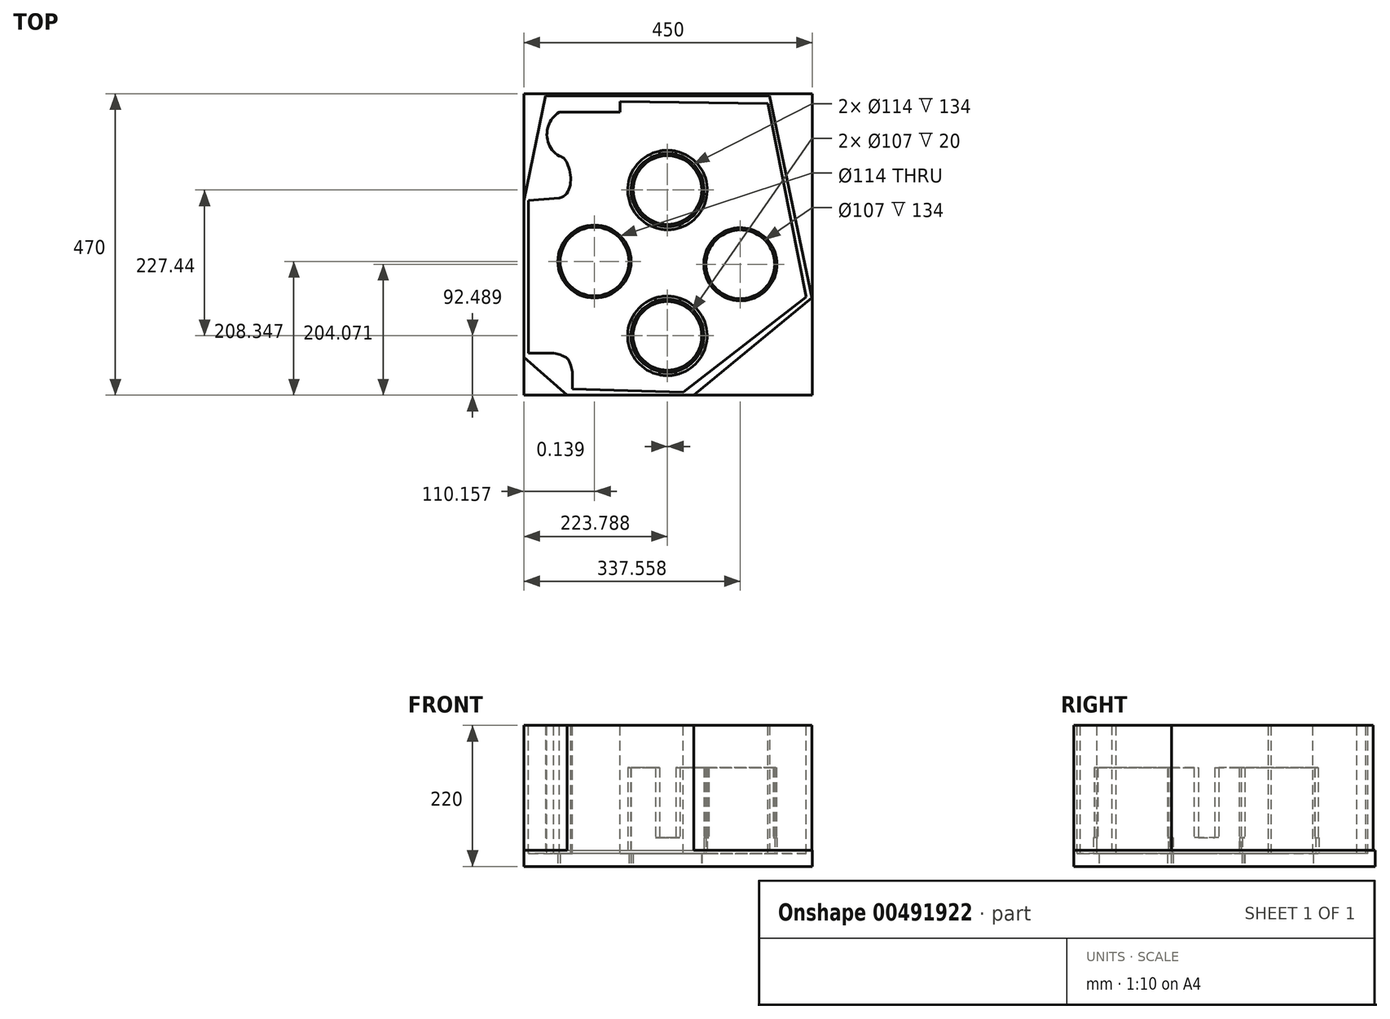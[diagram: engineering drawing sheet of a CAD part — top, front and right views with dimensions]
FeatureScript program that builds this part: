
annotation { "Feature Type Name" : "Feature", "Feature Type Description" : "" }
export const myFeature = defineFeature(function(context is Context, id is Id, definition is map)
    precondition{}
    {
        {
            var Q0;
            Q0=qCreatedBy(makeId("Top.planeOp"),FACE);
            var sketch = newSketch(context, id + "F0", { "sketchPlane" : qUnion([Q0])});
            skLineSegment(sketch, "E0", {"start": v(-238.56, 7.34) * mm, "end": v(-238.56, -236.7) * mm});
            skLineSegment(sketch, "E1", {"start": v(-171.3, -295.66) * mm, "end": v(26.17, -295.66) * mm});
            skLineSegment(sketch, "E2", {"start": v(-204.78, 171.15) * mm, "end": v(144.4, 171.15) * mm});
            skLineSegment(sketch, "E3", {"start": v(-238.56, 7.34) * mm, "end": v(-204.78, 171.15) * mm});
            skLineSegment(sketch, "E4", {"start": v(-238.56, -236.7) * mm, "end": v(-171.3, -295.66) * mm});
            skLineSegment(sketch, "E5", {"start": v(26.17, -295.66) * mm, "end": v(210.43, -143.64) * mm});
            skLineSegment(sketch, "E6", {"start": v(210.43, -143.64) * mm, "end": v(144.4, 171.15) * mm});
            skSolve(sketch);
        }
        {
            var Q0;
            Q0=qSketchRegion(id+"F0",true);
            extrude(context, id + "F1", {"entities" : qUnion([Q0]), "depth" : 220 * mm});
        }
        {
            var Q0;
            Q0=makeQuery(id+"F1.opExtrude","CAP_FACE",FACE,{"disambiguationData":[OSD([sQuery(id+"F0.wireOp",EDGE,"E0"),sQuery(id+"F0.wireOp",EDGE,"E1"),sQuery(id+"F0.wireOp",EDGE,"E2"),sQuery(id+"F0.wireOp",EDGE,"E3"),sQuery(id+"F0.wireOp",EDGE,"E4"),sQuery(id+"F0.wireOp",EDGE,"E5"),sQuery(id+"F0.wireOp",EDGE,"E6")])],"isStart":false});
            var sketch = newSketch(context, id + "F2", { "sketchPlane" : qUnion([Q0])});
            skLineSegment(sketch, "E7", {"start": v(-88.7, 162.55) * mm, "end": v(141.95, 159.17) * mm});
            skLineSegment(sketch, "E8", {"start": v(141.95, 159.17) * mm, "end": v(201.83, -142.4) * mm});
            skLineSegment(sketch, "E9", {"start": v(201.83, -142.4) * mm, "end": v(10.2, -291.05) * mm});
            skLineSegment(sketch, "E10", {"start": v(10.2, -291.05) * mm, "end": v(-163.01, -285.83) * mm});
            skLineSegment(sketch, "E11", {"start": v(-231.2, -229.93) * mm, "end": v(-231.2, 7.77) * mm});
            skLineSegment(sketch, "E12", {"start": v(-88.7, 162.55) * mm, "end": v(-88.7, 145.66) * mm});
            skLineSegment(sketch, "E13", {"start": v(-88.7, 145.66) * mm, "end": v(-182.98, 145.66) * mm});
            skFitSpline(sketch, "E14", {"points": [v(-182.98, 145.66) * mm, v(-182.98, 77.18) * mm], "startDerivative": vector(-73.7, -41.46) * mm, "endDerivative": vector(82.92, -44.22) * mm});
            skFitSpline(sketch, "E15", {"points": [v(-182.98, 77.18) * mm, v(-182.98, 12.07) * mm], "startDerivative": vector(54.36, -6.45) * mm, "endDerivative": vector(-83.84, -15.66) * mm});
            skLineSegment(sketch, "E16", {"start": v(-182.98, 12.07) * mm, "end": v(-231.2, 7.77) * mm});
            skLineSegment(sketch, "E17", {"start": v(-231.2, -229.93) * mm, "end": v(-191.88, -229.93) * mm});
            skLineSegment(sketch, "E18", {"start": v(-163.01, -285.83) * mm, "end": v(-163.01, -259.42) * mm});
            skFitSpline(sketch, "E19", {"points": [v(-191.88, -229.93) * mm, v(-163.01, -259.42) * mm], "startDerivative": vector(70.94, -20.27) * mm, "endDerivative": vector(15.66, -68.18) * mm});
            skSolve(sketch);
        }
        {
            var Q0;
            Q0=qCreatedBy(makeId("Top.planeOp"),FACE);
            var sketch = newSketch(context, id + "F3", { "sketchPlane" : qUnion([Q0])});
            skLineSegment(sketch, "E20.bottom", {"start": v(-238.56, -295.66) * mm, "end": v(211.44, -295.66) * mm});
            skLineSegment(sketch, "E20.top", {"start": v(-238.56, 174.34) * mm, "end": v(211.44, 174.34) * mm});
            skLineSegment(sketch, "E20.left", {"start": v(-238.56, -295.66) * mm, "end": v(-238.56, 174.34) * mm});
            skLineSegment(sketch, "E20.right", {"start": v(211.44, -295.66) * mm, "end": v(211.44, 174.34) * mm});
            skSolve(sketch);
        }
        {
            var Q0;
            Q0=makeQuery(id+"F3.imprint","IMPRINT",FACE,{"disambiguationData":[TD([[makeQuery(id+"F3.imprint","IMPRINT",EDGE,{"derivedFrom":sQuery(id+"F3.wireOp",EDGE,"E20.bottom")}),1.0]])]});
            extrude(context, id + "F4", {"entities" : qUnion([Q0]), "operationType" : NewBodyOperationType.ADD, "depth" : 25 * mm});
        }
        {
            var Q0;
            Q0=qSketchRegion(id+"F2",true);
            extrude(context, id + "F5", {"entities" : qUnion([Q0]), "operationType" : NewBodyOperationType.REMOVE, "oppositeDirection" : true, "depth" : 200 * mm});
        }
        {
            var Q0;
            Q0=qCreatedBy(makeId("Top.planeOp"),FACE);
            var sketch = newSketch(context, id + "F6", { "sketchPlane" : qUnion([Q0])});
            skCircle(sketch, "E21", {"center": v(-14.63, 24.27) * mm, "radius": 57 * mm});
            skCircle(sketch, "E22.0", {"center": v(-14.63, 24.27) * mm, "radius": 62 * mm});
            skLineSegment(sketch, "E23", {"start": v(-103, -176.05) * mm, "end": v(74.3, -2.16) * mm});
            skLineSegment(sketch, "E24", {"start": v(-102.43, 0) * mm, "end": v(76.04, -181.98) * mm});
            skCircle(sketch, "E25.MirrorC", {"center": v(99, -91.59) * mm, "radius": 57 * mm});
            skCircle(sketch, "E26.MirrorC", {"center": v(99, -91.59) * mm, "radius": 62 * mm});
            skCircle(sketch, "E27.MirrorC", {"center": v(-128.4, -87.31) * mm, "radius": 62 * mm});
            skCircle(sketch, "E28.MirrorC", {"center": v(-128.4, -87.31) * mm, "radius": 57 * mm});
            skCircle(sketch, "E29.MirrorC", {"center": v(-14.77, -203.17) * mm, "radius": 62 * mm});
            skCircle(sketch, "E30.MirrorC", {"center": v(-14.77, -203.17) * mm, "radius": 57 * mm});
            skCircle(sketch, "E31", {"center": v(-14.63, 24.27) * mm, "radius": 53.5 * mm});
            skCircle(sketch, "E32.MirrorC", {"center": v(-128.4, -87.31) * mm, "radius": 53.5 * mm});
            skCircle(sketch, "E33.MirrorC", {"center": v(99, -91.59) * mm, "radius": 53.5 * mm});
            skCircle(sketch, "E34.MirrorC", {"center": v(-14.77, -203.17) * mm, "radius": 53.5 * mm});
            skSolve(sketch);
        }
        {
            var Q0;
            Q0=makeQuery(id+"F6.imprint","IMPRINT",FACE,{"disambiguationData":[TD([[makeQuery(id+"F6.imprint","IMPRINT",EDGE,{"derivedFrom":sQuery(id+"F6.wireOp",EDGE,"E31")}),1.0]])]});
            var Q1;
            Q1=makeQuery(id+"F6.imprint","IMPRINT",FACE,{"disambiguationData":[TD([[makeQuery(id+"F6.imprint","IMPRINT",EDGE,{"derivedFrom":sQuery(id+"F6.wireOp",EDGE,"E32.MirrorC")}),-1.0]])]});
            var Q2;
            Q2=makeQuery(id+"F6.imprint","IMPRINT",FACE,{"disambiguationData":[TD([[makeQuery(id+"F6.imprint","IMPRINT",EDGE,{"derivedFrom":sQuery(id+"F6.wireOp",EDGE,"E34.MirrorC")}),1.0]])]});
            var Q3;
            Q3=makeQuery(id+"F6.imprint","IMPRINT",FACE,{"disambiguationData":[TD([[makeQuery(id+"F6.imprint","IMPRINT",EDGE,{"derivedFrom":sQuery(id+"F6.wireOp",EDGE,"E33.MirrorC")}),-1.0]])]});
            extrude(context, id + "F7", {"entities" : qUnion([Q0, Q1, Q2, Q3]), "operationType" : NewBodyOperationType.REMOVE, "endBound" : BoundingType.UP_TO_NEXT, "depth" : 25 * mm});
        }
        {
            var Q0;
            Q0=makeQuery(id+"F6.imprint","IMPRINT",FACE,{"disambiguationData":[TD([[makeQuery(id+"F6.imprint","IMPRINT",EDGE,{"derivedFrom":sQuery(id+"F6.wireOp",EDGE,"E25.MirrorC")}),1.0]])]});
            var Q1;
            Q1=makeQuery(id+"F6.imprint","IMPRINT",FACE,{"disambiguationData":[TD([[makeQuery(id+"F6.imprint","IMPRINT",EDGE,{"derivedFrom":sQuery(id+"F6.wireOp",EDGE,"E21")}),-1.0]])]});
            var Q2;
            Q2=makeQuery(id+"F6.imprint","IMPRINT",FACE,{"disambiguationData":[TD([[makeQuery(id+"F6.imprint","IMPRINT",EDGE,{"derivedFrom":sQuery(id+"F6.wireOp",EDGE,"E27.MirrorC")}),-1.0]])]});
            var Q3;
            Q3=makeQuery(id+"F6.imprint","IMPRINT",FACE,{"disambiguationData":[TD([[makeQuery(id+"F6.imprint","IMPRINT",EDGE,{"derivedFrom":sQuery(id+"F6.wireOp",EDGE,"E29.MirrorC")}),1.0]])]});
            extrude(context, id + "F8", {"entities" : qUnion([Q0, Q1, Q2, Q3]), "operationType" : NewBodyOperationType.ADD, "depth" : 154 * mm});
        }
        {
            var Q0;
            Q0=makeQuery(id+"F1.opExtrude","CAP_FACE",FACE,{"disambiguationData":[OSD([sQuery(id+"F0.wireOp",EDGE,"E0"),sQuery(id+"F0.wireOp",EDGE,"E1"),sQuery(id+"F0.wireOp",EDGE,"E2"),sQuery(id+"F0.wireOp",EDGE,"E3"),sQuery(id+"F0.wireOp",EDGE,"E4"),sQuery(id+"F0.wireOp",EDGE,"E5"),sQuery(id+"F0.wireOp",EDGE,"E6")])],"isStart":false});
            var sketch = newSketch(context, id + "F9", { "sketchPlane" : qUnion([Q0])});
            skLineSegment(sketch, "E35", {"start": v(-14.37, 55.87) * mm, "end": v(-14.37, -234.54) * mm, "construction": true});
            skLineSegment(sketch, "E36", {"start": v(-153.35, -89.05) * mm, "end": v(136.38, -89.05) * mm, "construction": true});
            skPoint(sketch, "E37.center", {"position": v(-14.37, -89.05) * mm});
            skLineSegment(sketch, "E38.bottom", {"start": v(-33.62, -89.05) * mm, "end": v(4.88, -89.05) * mm});
            skLineSegment(sketch, "E38.top", {"start": v(-33.62, 14.6) * mm, "end": v(4.88, 14.6) * mm});
            skLineSegment(sketch, "E38.left", {"start": v(-33.62, -89.05) * mm, "end": v(-33.62, 14.6) * mm});
            skLineSegment(sketch, "E38.right", {"start": v(4.88, -89.05) * mm, "end": v(4.88, 14.6) * mm});
            skLineSegment(sketch, "E39.bottom", {"start": v(-27.12, 14.6) * mm, "end": v(-1.62, 14.6) * mm});
            skLineSegment(sketch, "E39.top", {"start": v(-27.12, 104.97) * mm, "end": v(-1.62, 104.97) * mm});
            skLineSegment(sketch, "E39.left", {"start": v(-27.12, 14.6) * mm, "end": v(-27.12, 104.97) * mm});
            skLineSegment(sketch, "E39.right", {"start": v(-1.62, 14.6) * mm, "end": v(-1.62, 104.97) * mm});
            skLineSegment(sketch, "E40.1.0", {"start": v(-118.03, -101.8) * mm, "end": v(-208.39, -101.8) * mm});
            skLineSegment(sketch, "E40.1.1", {"start": v(-208.39, -101.8) * mm, "end": v(-208.39, -76.3) * mm});
            skLineSegment(sketch, "E40.1.2", {"start": v(-118.03, -76.3) * mm, "end": v(-208.39, -76.3) * mm});
            skLineSegment(sketch, "E40.1.3", {"start": v(-118.03, -101.8) * mm, "end": v(-118.03, -76.3) * mm});
            skLineSegment(sketch, "E40.1.4", {"start": v(-14.37, -108.3) * mm, "end": v(-118.03, -108.3) * mm});
            skLineSegment(sketch, "E40.1.5", {"start": v(-14.37, -69.8) * mm, "end": v(-118.03, -69.8) * mm});
            skLineSegment(sketch, "E40.1.6", {"start": v(-118.03, -108.3) * mm, "end": v(-118.03, -69.8) * mm});
            skLineSegment(sketch, "E40.1.8", {"start": v(-14.37, -108.3) * mm, "end": v(-14.37, -69.8) * mm});
            skLineSegment(sketch, "E40.2.0", {"start": v(-1.63, -192.7) * mm, "end": v(-1.63, -283.06) * mm});
            skLineSegment(sketch, "E40.2.1", {"start": v(-1.63, -283.06) * mm, "end": v(-27.13, -283.06) * mm});
            skLineSegment(sketch, "E40.2.2", {"start": v(-27.13, -192.7) * mm, "end": v(-27.13, -283.06) * mm});
            skLineSegment(sketch, "E40.2.3", {"start": v(-1.63, -192.7) * mm, "end": v(-27.13, -192.7) * mm});
            skLineSegment(sketch, "E40.2.4", {"start": v(4.87, -89.05) * mm, "end": v(4.87, -192.7) * mm});
            skLineSegment(sketch, "E40.2.5", {"start": v(-33.63, -89.05) * mm, "end": v(-33.63, -192.7) * mm});
            skLineSegment(sketch, "E40.2.6", {"start": v(4.87, -192.7) * mm, "end": v(-33.63, -192.7) * mm});
            skLineSegment(sketch, "E40.2.8", {"start": v(4.87, -89.05) * mm, "end": v(-33.63, -89.05) * mm});
            skLineSegment(sketch, "E40.3.0", {"start": v(89.28, -76.3) * mm, "end": v(179.64, -76.3) * mm});
            skLineSegment(sketch, "E40.3.1", {"start": v(179.64, -76.3) * mm, "end": v(179.64, -101.8) * mm});
            skLineSegment(sketch, "E40.3.2", {"start": v(89.28, -101.8) * mm, "end": v(179.64, -101.8) * mm});
            skLineSegment(sketch, "E40.3.3", {"start": v(89.28, -76.3) * mm, "end": v(89.28, -101.8) * mm});
            skLineSegment(sketch, "E40.3.4", {"start": v(-14.37, -69.8) * mm, "end": v(89.28, -69.8) * mm});
            skLineSegment(sketch, "E40.3.5", {"start": v(-14.37, -108.3) * mm, "end": v(89.28, -108.3) * mm});
            skLineSegment(sketch, "E40.3.6", {"start": v(89.28, -69.8) * mm, "end": v(89.28, -108.3) * mm});
            skLineSegment(sketch, "E40.3.8", {"start": v(-14.37, -69.8) * mm, "end": v(-14.37, -108.3) * mm});
            skSolve(sketch);
        }
        {
            var Q0;
            Q0=qSketchRegion(id+"F9",true);
            extrude(context, id + "F10", {"entities" : qUnion([Q0]), "operationType" : NewBodyOperationType.REMOVE, "oppositeDirection" : true, "depth" : 175 * mm});
        }
    });
